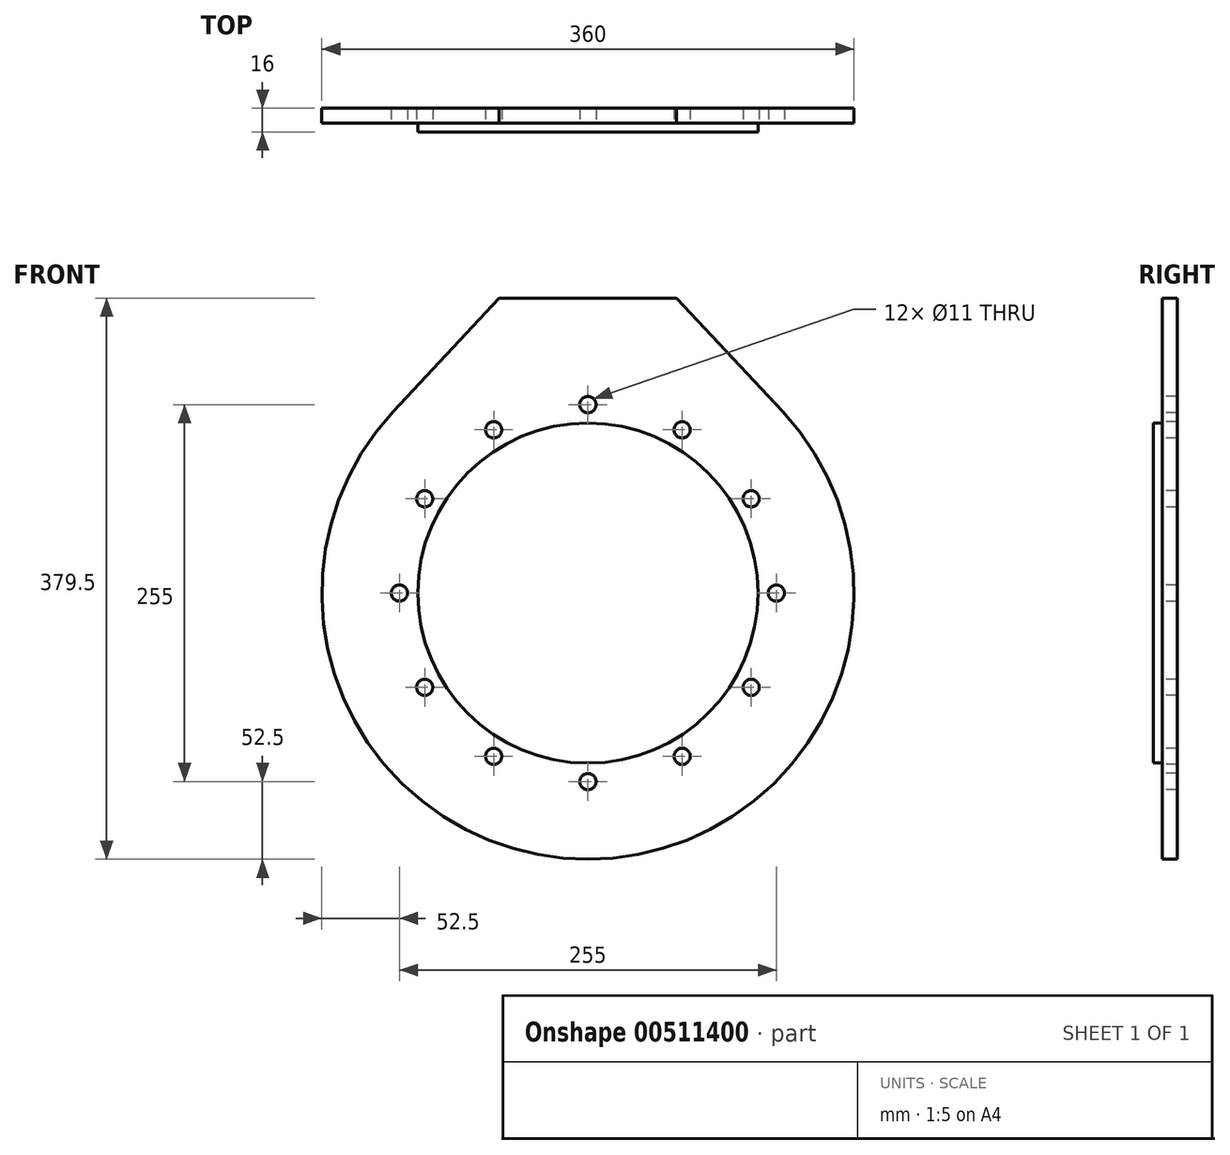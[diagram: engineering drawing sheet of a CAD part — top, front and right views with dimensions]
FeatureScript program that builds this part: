
annotation { "Feature Type Name" : "Feature", "Feature Type Description" : "" }
export const myFeature = defineFeature(function(context is Context, id is Id, definition is map)
    precondition{}
    {
        {
            var Q0;
            Q0=qCreatedBy(makeId("Front.planeOp"),FACE);
            var sketch = newSketch(context, id + "F0", { "sketchPlane" : qUnion([Q0])});
            skArc(sketch, "E0", {"start": v(-131.57, 122.84) * mm, "mid": v(0, -180) * mm, "end": v(131.57, 122.84) * mm});
            skLineSegment(sketch, "E1", {"start": v(0, 0) * mm, "end": v(0, 199.5) * mm, "construction": true});
            skLineSegment(sketch, "E2", {"start": v(0, 199.5) * mm, "end": v(-60, 199.5) * mm});
            skLineSegment(sketch, "E3", {"start": v(-60, 199.5) * mm, "end": v(-131.57, 122.84) * mm});
            skLineSegment(sketch, "E4", {"start": v(0, 199.5) * mm, "end": v(60, 199.5) * mm});
            skLineSegment(sketch, "E5", {"start": v(60, 199.5) * mm, "end": v(131.57, 122.84) * mm});
            skSolve(sketch);
        }
        {
            var Q0;
            Q0 = qSketchRegion(id + "F0", true);
            extrude(context, id + "F1", {"entities" : qUnion([Q0]), "oppositeDirection" : true, "depth" : 10 * mm});
        }
        {
            var Q0;
            Q0=makeQuery(id+"F1.opExtrude","CAP_FACE",FACE,{"disambiguationData":[OSD([sQuery(id+"F0.wireOp",EDGE,"E0"),sQuery(id+"F0.wireOp",EDGE,"E2"),sQuery(id+"F0.wireOp",EDGE,"E3"),sQuery(id+"F0.wireOp",EDGE,"E4"),sQuery(id+"F0.wireOp",EDGE,"E5")])],"isStart":true});
            var sketch = newSketch(context, id + "F2", { "sketchPlane" : qUnion([Q0])});
            skCircle(sketch, "E6", {"center": v(0, 199.5) * mm, "radius": 60 * mm});
            skSolve(sketch);
        }
        {
            var Q0;
            {var subQ1=makeQuery(id+"F1.opExtrude","CAP_EDGE",EDGE,{"disambiguationData":[OSD([sQuery(id+"F0.wireOp",EDGE,"E2"),sQuery(id+"F0.wireOp",EDGE,"E4")])],"isStart":true});Q0=makeQuery(id+"F2.imprint","IMPRINT",FACE,{"disambiguationData":[TD([[makeQuery(id+"F2.imprint","IMPRINT",EDGE,{"derivedFrom":subQ1}),-1.0]])]});}
            var Q1;
            Q1=makeQuery(id+"F1.opExtrude","CAP_FACE",FACE,{"disambiguationData":[OSD([sQuery(id+"F0.wireOp",EDGE,"E0"),sQuery(id+"F0.wireOp",EDGE,"E2"),sQuery(id+"F0.wireOp",EDGE,"E3"),sQuery(id+"F0.wireOp",EDGE,"E4"),sQuery(id+"F0.wireOp",EDGE,"E5")])],"isStart":false});
            extrude(context, id + "F3", {"entities" : qUnion([Q0]), "operationType" : NewBodyOperationType.REMOVE, "endBound" : BoundingType.UP_TO_SURFACE, "oppositeDirection" : true, "endBoundEntityFace" : qUnion([Q1]), "depth" : 25 * mm});
        }
        {
            var Q0;
            Q0=makeQuery(id+"F1.opExtrude","CAP_FACE",FACE,{"disambiguationData":[OSD([sQuery(id+"F0.wireOp",EDGE,"E0"),sQuery(id+"F0.wireOp",EDGE,"E2"),sQuery(id+"F0.wireOp",EDGE,"E3"),sQuery(id+"F0.wireOp",EDGE,"E4"),sQuery(id+"F0.wireOp",EDGE,"E5")])],"isStart":true});
            var sketch = newSketch(context, id + "F4", { "sketchPlane" : qUnion([Q0])});
            skCircle(sketch, "E7", {"center": v(0, 0) * mm, "radius": 115 * mm});
            skSolve(sketch);
        }
        {
            var Q0;
            Q0=makeQuery(id+"F4.imprint","IMPRINT",FACE,{"disambiguationData":[TD([[makeQuery(id+"F4.imprint","IMPRINT",EDGE,{"derivedFrom":sQuery(id+"F4.wireOp",EDGE,"E7")}),1.0]])]});
            extrude(context, id + "F5", {"entities" : qUnion([Q0]), "operationType" : NewBodyOperationType.ADD, "depth" : 6 * mm});
        }
        {
            var Q0;
            Q0=makeQuery(id+"F1.opExtrude","CAP_FACE",FACE,{"disambiguationData":[OSD([sQuery(id+"F0.wireOp",EDGE,"E0"),sQuery(id+"F0.wireOp",EDGE,"E2"),sQuery(id+"F0.wireOp",EDGE,"E3"),sQuery(id+"F0.wireOp",EDGE,"E4"),sQuery(id+"F0.wireOp",EDGE,"E5")])],"isStart":true});
            var sketch = newSketch(context, id + "F6", { "sketchPlane" : qUnion([Q0])});
            skCircle(sketch, "E8", {"center": v(0, 0) * mm, "radius": 127.5 * mm, "construction": true});
            skLineSegment(sketch, "E9", {"start": v(0, 0) * mm, "end": v(0, 127.5) * mm, "construction": true});
            skCircle(sketch, "E10", {"center": v(0, 127.5) * mm, "radius": 5.5 * mm});
            skCircle(sketch, "E11.1.0", {"center": v(63.75, 110.42) * mm, "radius": 5.5 * mm});
            skCircle(sketch, "E11.2.0", {"center": v(110.42, 63.75) * mm, "radius": 5.5 * mm});
            skCircle(sketch, "E11.3.0", {"center": v(127.5, 0) * mm, "radius": 5.5 * mm});
            skCircle(sketch, "E11.4.0", {"center": v(110.42, -63.75) * mm, "radius": 5.5 * mm});
            skCircle(sketch, "E11.5.0", {"center": v(63.75, -110.42) * mm, "radius": 5.5 * mm});
            skCircle(sketch, "E11.6.0", {"center": v(0, -127.5) * mm, "radius": 5.5 * mm});
            skCircle(sketch, "E11.7.0", {"center": v(-63.75, -110.42) * mm, "radius": 5.5 * mm});
            skCircle(sketch, "E11.8.0", {"center": v(-110.42, -63.75) * mm, "radius": 5.5 * mm});
            skCircle(sketch, "E11.9.0", {"center": v(-127.5, 0) * mm, "radius": 5.5 * mm});
            skCircle(sketch, "E11.10.0", {"center": v(-110.42, 63.75) * mm, "radius": 5.5 * mm});
            skCircle(sketch, "E11.11.0", {"center": v(-63.75, 110.42) * mm, "radius": 5.5 * mm});
            skLineSegment(sketch, "E11.anchor2", {"start": v(0, 0) * mm, "end": v(-63.75, 110.42) * mm, "construction": true});
            skSolve(sketch);
        }
        {
            var Q0;
            Q0=makeQuery(id+"F6.imprint","IMPRINT",FACE,{"disambiguationData":[TD([[makeQuery(id+"F6.imprint","IMPRINT",EDGE,{"derivedFrom":sQuery(id+"F6.wireOp",EDGE,"E11.11.0")}),1.0]])]});
            var Q1;
            Q1=makeQuery(id+"F6.imprint","IMPRINT",FACE,{"disambiguationData":[TD([[makeQuery(id+"F6.imprint","IMPRINT",EDGE,{"derivedFrom":sQuery(id+"F6.wireOp",EDGE,"E10")}),1.0]])]});
            var Q2;
            Q2=makeQuery(id+"F6.imprint","IMPRINT",FACE,{"disambiguationData":[TD([[makeQuery(id+"F6.imprint","IMPRINT",EDGE,{"derivedFrom":sQuery(id+"F6.wireOp",EDGE,"E11.1.0")}),1.0]])]});
            var Q3;
            Q3=makeQuery(id+"F6.imprint","IMPRINT",FACE,{"disambiguationData":[TD([[makeQuery(id+"F6.imprint","IMPRINT",EDGE,{"derivedFrom":sQuery(id+"F6.wireOp",EDGE,"E11.2.0")}),1.0]])]});
            var Q4;
            Q4=makeQuery(id+"F6.imprint","IMPRINT",FACE,{"disambiguationData":[TD([[makeQuery(id+"F6.imprint","IMPRINT",EDGE,{"derivedFrom":sQuery(id+"F6.wireOp",EDGE,"E11.3.0")}),1.0]])]});
            var Q5;
            Q5=makeQuery(id+"F6.imprint","IMPRINT",FACE,{"disambiguationData":[TD([[makeQuery(id+"F6.imprint","IMPRINT",EDGE,{"derivedFrom":sQuery(id+"F6.wireOp",EDGE,"E11.4.0")}),1.0]])]});
            var Q6;
            Q6=makeQuery(id+"F6.imprint","IMPRINT",FACE,{"disambiguationData":[TD([[makeQuery(id+"F6.imprint","IMPRINT",EDGE,{"derivedFrom":sQuery(id+"F6.wireOp",EDGE,"E11.5.0")}),1.0]])]});
            var Q7;
            Q7=makeQuery(id+"F6.imprint","IMPRINT",FACE,{"disambiguationData":[TD([[makeQuery(id+"F6.imprint","IMPRINT",EDGE,{"derivedFrom":sQuery(id+"F6.wireOp",EDGE,"E11.6.0")}),1.0]])]});
            var Q8;
            Q8=makeQuery(id+"F6.imprint","IMPRINT",FACE,{"disambiguationData":[TD([[makeQuery(id+"F6.imprint","IMPRINT",EDGE,{"derivedFrom":sQuery(id+"F6.wireOp",EDGE,"E11.7.0")}),1.0]])]});
            var Q9;
            Q9=makeQuery(id+"F6.imprint","IMPRINT",FACE,{"disambiguationData":[TD([[makeQuery(id+"F6.imprint","IMPRINT",EDGE,{"derivedFrom":sQuery(id+"F6.wireOp",EDGE,"E11.8.0")}),1.0]])]});
            var Q10;
            Q10=makeQuery(id+"F6.imprint","IMPRINT",FACE,{"disambiguationData":[TD([[makeQuery(id+"F6.imprint","IMPRINT",EDGE,{"derivedFrom":sQuery(id+"F6.wireOp",EDGE,"E11.9.0")}),1.0]])]});
            var Q11;
            Q11=makeQuery(id+"F6.imprint","IMPRINT",FACE,{"disambiguationData":[TD([[makeQuery(id+"F6.imprint","IMPRINT",EDGE,{"derivedFrom":sQuery(id+"F6.wireOp",EDGE,"E11.10.0")}),1.0]])]});
            var Q12;
            Q12=makeQuery(id+"F1.opExtrude","CAP_FACE",FACE,{"disambiguationData":[OSD([sQuery(id+"F0.wireOp",EDGE,"E0"),sQuery(id+"F0.wireOp",EDGE,"E2"),sQuery(id+"F0.wireOp",EDGE,"E3"),sQuery(id+"F0.wireOp",EDGE,"E4"),sQuery(id+"F0.wireOp",EDGE,"E5")])],"isStart":false});
            extrude(context, id + "F7", {"entities" : qUnion([Q0, Q1, Q2, Q3, Q4, Q5, Q6, Q7, Q8, Q9, Q10, Q11]), "operationType" : NewBodyOperationType.REMOVE, "endBound" : BoundingType.UP_TO_SURFACE, "oppositeDirection" : true, "endBoundEntityFace" : qUnion([Q12]), "depth" : 25 * mm});
        }
    });
